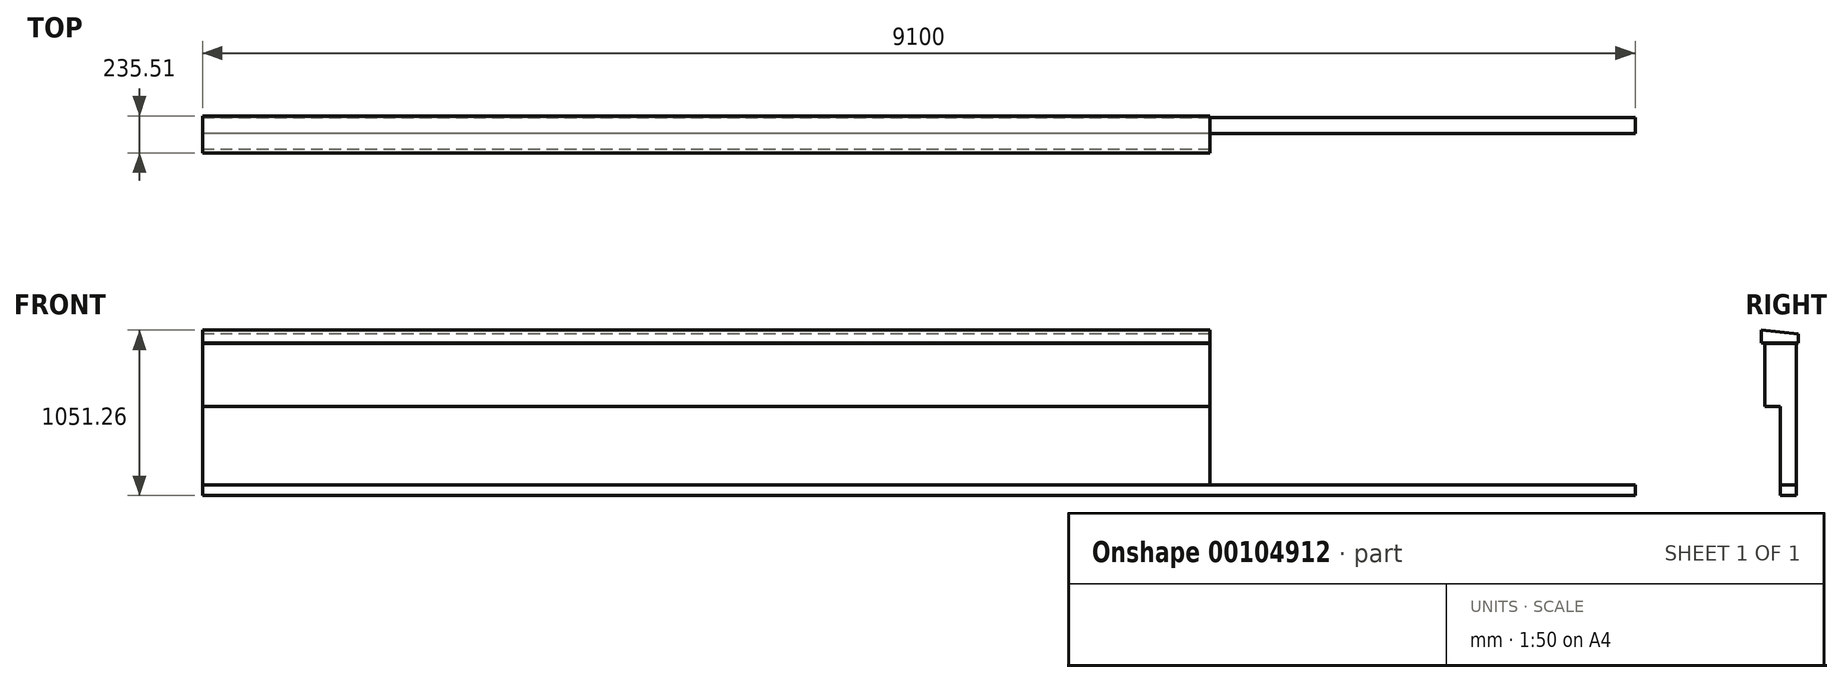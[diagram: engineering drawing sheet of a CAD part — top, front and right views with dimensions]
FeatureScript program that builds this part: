
annotation { "Feature Type Name" : "Feature", "Feature Type Description" : "" }
export const myFeature = defineFeature(function(context is Context, id is Id, definition is map)
    precondition{}
    {
        {
            var Q0;
            Q0=qCreatedBy(makeId("Right.planeOp"),FACE);
            var sketch = newSketch(context, id + "F0", { "sketchPlane" : qUnion([Q0])});
            skLineSegment(sketch, "E0.top", {"start": v(-100, -294.93) * mm, "end": v(0, -294.93) * mm});
            skLineSegment(sketch, "E0.left", {"start": v(-100, 105.07) * mm, "end": v(-100, -294.93) * mm});
            skLineSegment(sketch, "E0.right", {"start": v(100, 105.07) * mm, "end": v(100, -294.93) * mm});
            skLineSegment(sketch, "E1.left", {"start": v(100, -294.93) * mm, "end": v(100, -794.93) * mm});
            skLineSegment(sketch, "E1.right", {"start": v(0, -294.93) * mm, "end": v(0, -794.93) * mm});
            skLineSegment(sketch, "E2", {"start": v(-100, 105.07) * mm, "end": v(100, 105.07) * mm});
            skLineSegment(sketch, "E3", {"start": v(0, -794.93) * mm, "end": v(100, -794.93) * mm});
            skSolve(sketch);
        }
        {
            var Q0;
            Q0=qCreatedBy(makeId("Right.planeOp"),FACE);
            var sketch = newSketch(context, id + "F1", { "sketchPlane" : qUnion([Q0])});
            skLineSegment(sketch, "E4.bottom", {"start": v(-123.03, 107.28) * mm, "end": v(112.48, 107.28) * mm});
            skLineSegment(sketch, "E4.left", {"start": v(-123.03, 107.28) * mm, "end": v(-123.03, 190.08) * mm});
            skLineSegment(sketch, "E4.right", {"start": v(112.48, 107.28) * mm, "end": v(112.48, 163.95) * mm});
            skLineSegment(sketch, "E5", {"start": v(-123.03, 190.08) * mm, "end": v(112.48, 163.95) * mm});
            skSolve(sketch);
        }
        {
            var Q0;
            Q0=qCreatedBy(makeId("Right.planeOp"),FACE);
            var sketch = newSketch(context, id + "F2", { "sketchPlane" : qUnion([Q0])});
            skLineSegment(sketch, "E6.bottom", {"start": v(0, -794.51) * mm, "end": v(100.72, -794.51) * mm});
            skLineSegment(sketch, "E6.top", {"start": v(0, -861.18) * mm, "end": v(100.72, -861.18) * mm});
            skLineSegment(sketch, "E6.left", {"start": v(0, -794.51) * mm, "end": v(0, -861.18) * mm});
            skLineSegment(sketch, "E6.right", {"start": v(100.72, -794.51) * mm, "end": v(100.72, -861.18) * mm});
            skSolve(sketch);
        }
        {
            var Q0;
            Q0=qSketchRegion(id+"F0",true);
            extrude(context, id + "F3", {"entities" : qUnion([Q0]), "depth" : 6400 * mm});
        }
        {
            var Q0;
            Q0=qSketchRegion(id+"F1",true);
            extrude(context, id + "F4", {"entities" : qUnion([Q0]), "depth" : 6400 * mm});
        }
        {
            var Q0;
            Q0=qSketchRegion(id+"F2",true);
            extrude(context, id + "F5", {"entities" : qUnion([Q0]), "depth" : 9100 * mm});
        }
    });
